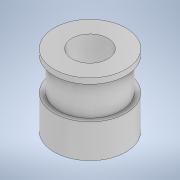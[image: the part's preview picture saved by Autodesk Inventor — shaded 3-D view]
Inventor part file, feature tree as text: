
AUTODESK INVENTOR PART (.ipt)
format: ipt  version: 2021 (Build 250183000, 183)  size: 116,736 bytes
history: native  units: mm
features: extrude x2, sketch x2, plane x1
ambient origin geometry x8: Origin, YZ Plane, XZ Plane, XY Plane, X Axis, Y Axis, Z Axis, Center Point
bodies: Solid1 (feature_tree)
feature tree (5):
  extrude  "Extrusion1"  Depth=8.0mm
  plane  "Work Plane1"
  extrude  "Extrusion2"  [1 undecoded]
  sketch  "Sketch1"  dims[d0=16.0mm d1=8.0mm]
  sketch  "Sketch2"  dims[d2=16.0mm d3=0.0mm d4=-1.25mm d5=1.0mm d6=7.25mm d7=0.0mm]
note: 1 required parameter value undecoded (feature->parameter linkage not recoverable at this tier; creation-order binding heuristic only, values carry confidence <= 0.55)
